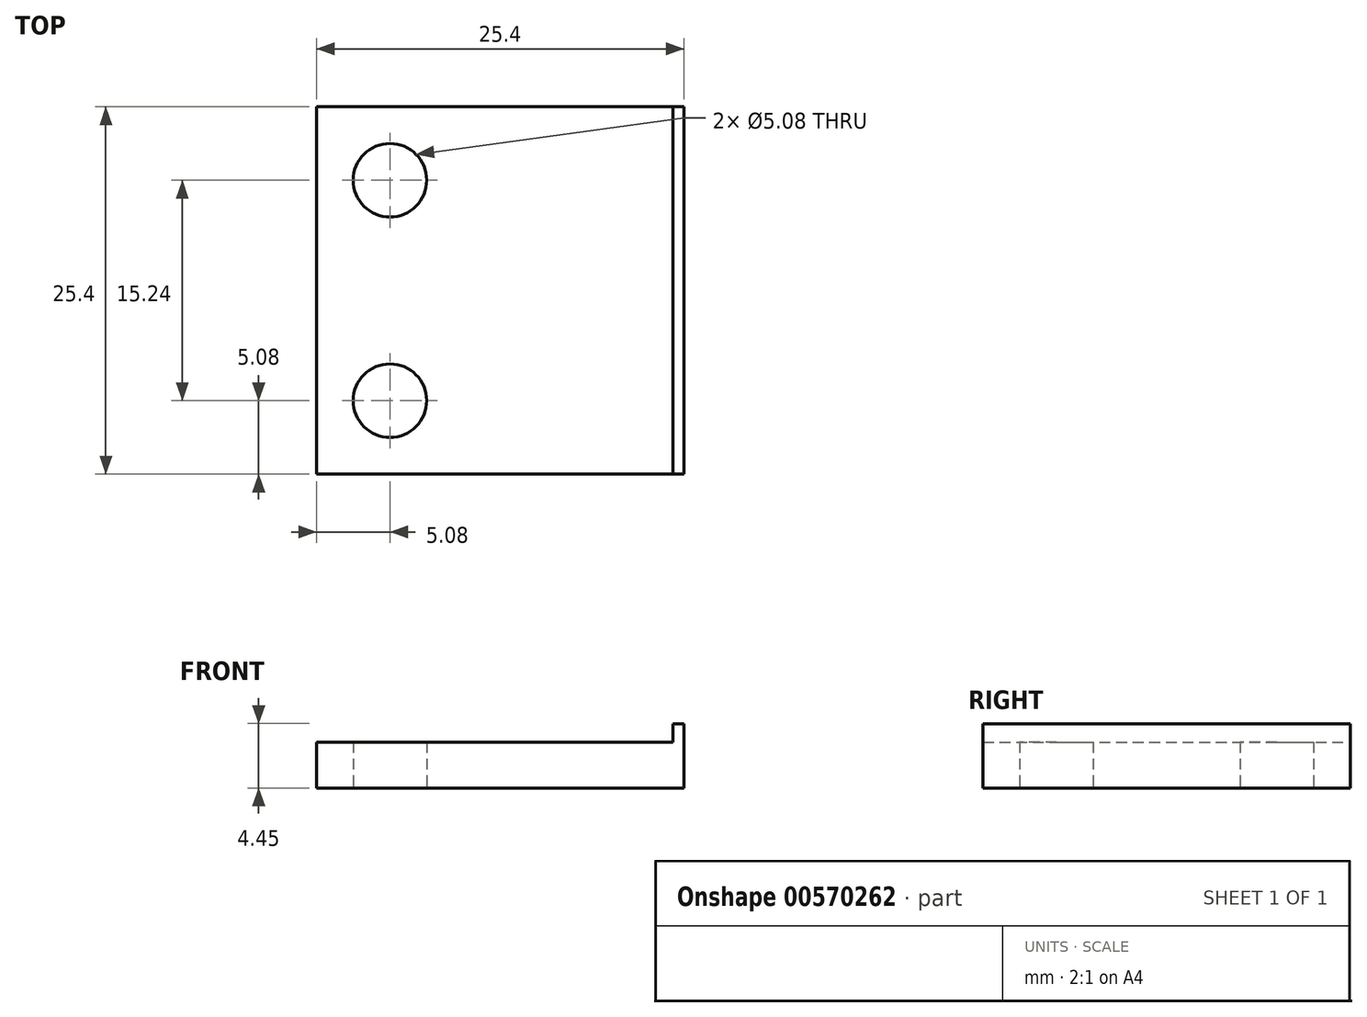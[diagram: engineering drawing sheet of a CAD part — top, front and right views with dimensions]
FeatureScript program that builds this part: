
annotation { "Feature Type Name" : "Feature", "Feature Type Description" : "" }
export const myFeature = defineFeature(function(context is Context, id is Id, definition is map)
    precondition{}
    {
        {
            var Q0;
            Q0=qCreatedBy(makeId("Front.planeOp"),FACE);
            var sketch = newSketch(context, id + "F0", { "sketchPlane" : qUnion([Q0])});
            skLineSegment(sketch, "E0.bottom", {"start": v(-12.7, 1.59) * mm, "end": v(12.7, 1.59) * mm});
            skLineSegment(sketch, "E0.top", {"start": v(-12.7, -1.59) * mm, "end": v(12.7, -1.59) * mm});
            skLineSegment(sketch, "E0.left", {"start": v(-12.7, 1.59) * mm, "end": v(-12.7, -1.59) * mm});
            skLineSegment(sketch, "E0.right", {"start": v(12.7, 1.59) * mm, "end": v(12.7, -1.59) * mm});
            skPoint(sketch, "E0.middle", {"position": v(0, 0) * mm});
            skLineSegment(sketch, "E1.bottom", {"start": v(12.7, 1.59) * mm, "end": v(11.94, 1.59) * mm});
            skLineSegment(sketch, "E1.top", {"start": v(12.7, 2.86) * mm, "end": v(11.94, 2.86) * mm});
            skLineSegment(sketch, "E1.left", {"start": v(12.7, 1.59) * mm, "end": v(12.7, 2.86) * mm});
            skLineSegment(sketch, "E1.right", {"start": v(11.94, 1.59) * mm, "end": v(11.94, 2.86) * mm});
            skSolve(sketch);
        }
        {
            var Q0;
            Q0 = qSketchRegion(id + "F0", true);
            extrude(context, id + "F1", {"entities" : qUnion([Q0]), "endBound" : BoundingType.SYMMETRIC, "depth" : 25.4 * mm, "offsetDistance" : 25.4 * mm});
        }
        {
            var Q0;
            Q0=makeQuery(id+"F1.opExtrude","SWEPT_FACE",FACE,{"disambiguationData":[OSD([sQuery(id+"F0.wireOp",EDGE,"E0.top")])]});
            var sketch = newSketch(context, id + "F2", { "sketchPlane" : qUnion([Q0])});
            skCircle(sketch, "E2", {"center": v(-7.62, 7.62) * mm, "radius": 2.54 * mm});
            skCircle(sketch, "E3", {"center": v(-7.62, -7.62) * mm, "radius": 2.54 * mm});
            skSolve(sketch);
        }
        {
            var Q0;
            Q0=makeQuery(id+"F2.imprint","IMPRINT",FACE,{"disambiguationData":[TD([[makeQuery(id+"F2.imprint","IMPRINT",EDGE,{"derivedFrom":sQuery(id+"F2.wireOp",EDGE,"E2")}),1.0]])]});
            var Q1;
            Q1=makeQuery(id+"F2.imprint","IMPRINT",FACE,{"disambiguationData":[TD([[makeQuery(id+"F2.imprint","IMPRINT",EDGE,{"derivedFrom":sQuery(id+"F2.wireOp",EDGE,"E3")}),1.0]])]});
            extrude(context, id + "F3", {"entities" : qUnion([Q0, Q1]), "operationType" : NewBodyOperationType.REMOVE, "endBound" : BoundingType.THROUGH_ALL, "oppositeDirection" : true, "depth" : 6.35 * mm, "offsetDistance" : 25.4 * mm});
        }
    });
